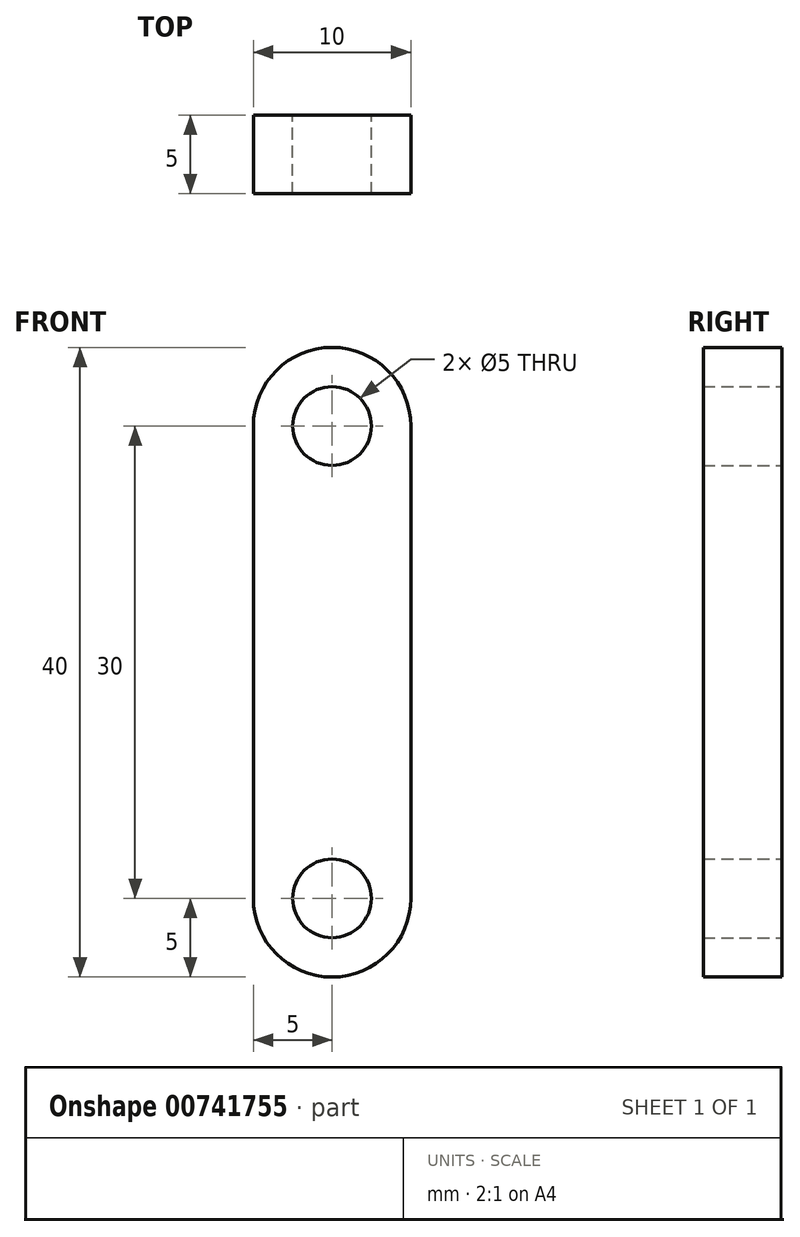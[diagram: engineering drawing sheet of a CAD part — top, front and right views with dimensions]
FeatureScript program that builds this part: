
annotation { "Feature Type Name" : "Feature", "Feature Type Description" : "" }
export const myFeature = defineFeature(function(context is Context, id is Id, definition is map)
    precondition{}
    {
        {
            var Q0;
            Q0=qCreatedBy(makeId("Front.planeOp"),FACE);
            var sketch = newSketch(context, id + "F0", { "sketchPlane" : qUnion([Q0])});
            skCircle(sketch, "E0", {"center": v(0, 0) * mm, "radius": 5 * mm});
            skCircle(sketch, "E1", {"center": v(0, 30) * mm, "radius": 5 * mm});
            skLineSegment(sketch, "E2", {"start": v(-5, 30) * mm, "end": v(-5, 0) * mm});
            skLineSegment(sketch, "E3", {"start": v(5, 30) * mm, "end": v(5, 0) * mm});
            skCircle(sketch, "E4", {"center": v(0, 30) * mm, "radius": 2.5 * mm});
            skCircle(sketch, "E5", {"center": v(0, 0) * mm, "radius": 2.5 * mm});
            skSolve(sketch);
        }
        {
            var Q0;
            {var subQ0=sQuery(id+"F0.wireOp",EDGE,"E2");Q0=makeQuery(id+"F0.imprint","IMPRINT",FACE,{"disambiguationData":[TD([[makeQuery(id+"F0.imprint","IMPRINT",EDGE,{"derivedFrom":subQ0}),1.0]])]});}
            var Q1;
            Q1=makeQuery(id+"F0.imprint","IMPRINT",FACE,{"disambiguationData":[TD([[makeQuery(id+"F0.imprint","IMPRINT",EDGE,{"derivedFrom":sQuery(id+"F0.wireOp",EDGE,"E4")}),-1.0]])]});
            var Q2;
            Q2=makeQuery(id+"F0.imprint","IMPRINT",FACE,{"disambiguationData":[TD([[makeQuery(id+"F0.imprint","IMPRINT",EDGE,{"derivedFrom":sQuery(id+"F0.wireOp",EDGE,"E5")}),-1.0]])]});
            extrude(context, id + "F1", {"entities" : qUnion([Q0, Q1, Q2]), "depth" : 5 * mm, "offsetDistance" : 25 * mm});
        }
    });
